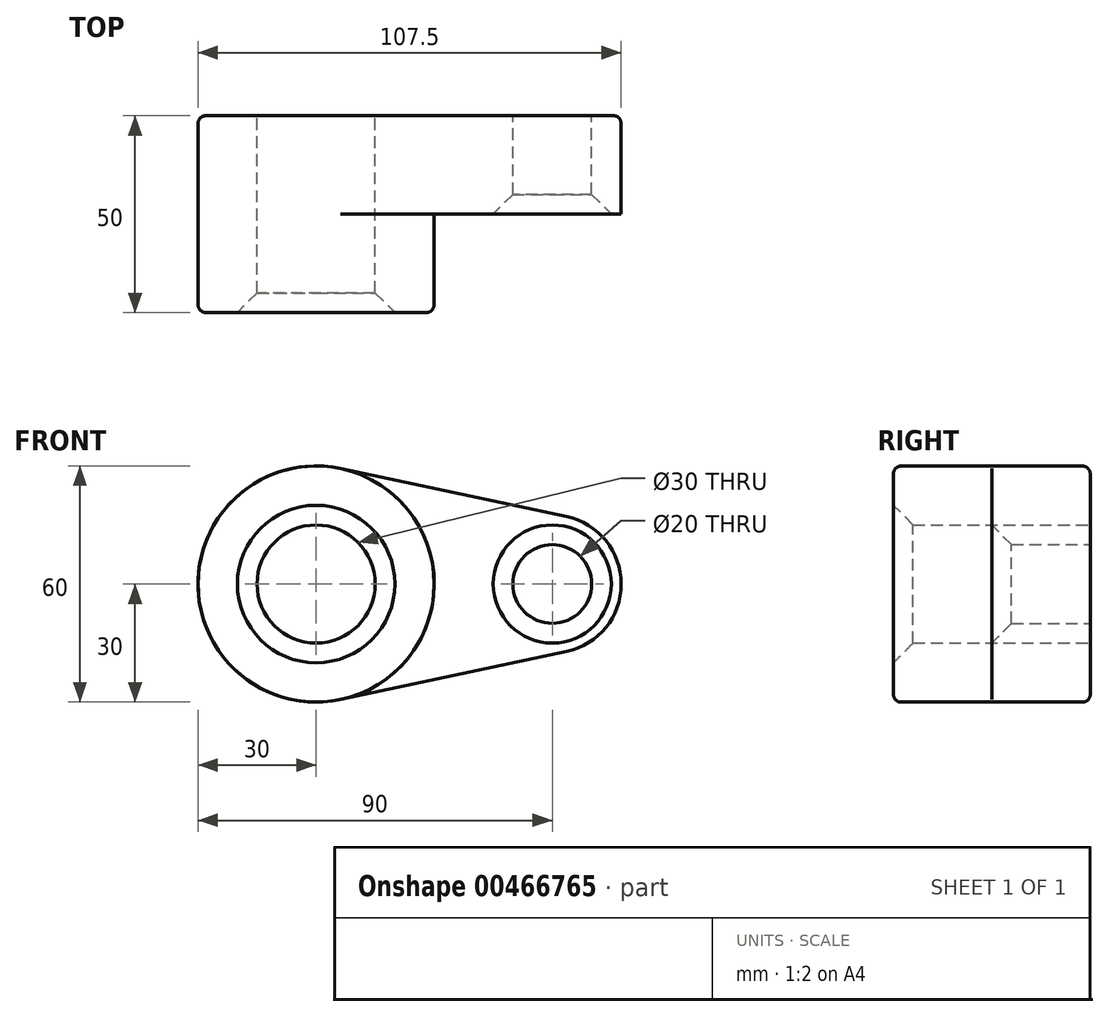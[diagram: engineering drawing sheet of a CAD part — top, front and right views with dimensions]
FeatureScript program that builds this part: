
annotation { "Feature Type Name" : "Feature", "Feature Type Description" : "" }
export const myFeature = defineFeature(function(context is Context, id is Id, definition is map)
    precondition{}
    {
        {
            var Q0;
            Q0=qCreatedBy(makeId("Front.planeOp"),FACE);
            var sketch = newSketch(context, id + "F0", { "sketchPlane" : qUnion([Q0])});
            skCircle(sketch, "E0", {"center": v(0, 0) * mm, "radius": 30 * mm});
            skCircle(sketch, "E1", {"center": v(60, 0) * mm, "radius": 17.5 * mm});
            skLineSegment(sketch, "E2", {"start": v(6.25, 29.34) * mm, "end": v(63.65, 17.12) * mm});
            skLineSegment(sketch, "E3", {"start": v(6.25, -29.34) * mm, "end": v(63.65, -17.12) * mm});
            skCircle(sketch, "E4", {"center": v(0, 0) * mm, "radius": 15 * mm});
            skCircle(sketch, "E5", {"center": v(60, 0) * mm, "radius": 10 * mm});
            skSolve(sketch);
        }
        {
            var Q0;
            Q0=makeQuery(id+"F0.imprint","IMPRINT",FACE,{"disambiguationData":[TD([[makeQuery(id+"F0.imprint","IMPRINT",EDGE,{"derivedFrom":sQuery(id+"F0.wireOp",EDGE,"E4")}),-1.0]])]});
            var Q1;
            {var subQ0=sQuery(id+"F0.wireOp",EDGE,"E2");Q1=makeQuery(id+"F0.imprint","IMPRINT",FACE,{"disambiguationData":[TD([[makeQuery(id+"F0.imprint","IMPRINT",EDGE,{"derivedFrom":subQ0}),-1.0]])]});}
            var Q2;
            Q2=makeQuery(id+"F0.imprint","IMPRINT",FACE,{"disambiguationData":[TD([[makeQuery(id+"F0.imprint","IMPRINT",EDGE,{"derivedFrom":sQuery(id+"F0.wireOp",EDGE,"E5")}),-1.0]])]});
            extrude(context, id + "F1", {"entities" : qUnion([Q0, Q1, Q2]), "depth" : 25 * mm});
        }
        {
            var Q0;
            Q0=makeQuery(id+"F0.imprint","IMPRINT",FACE,{"disambiguationData":[TD([[makeQuery(id+"F0.imprint","IMPRINT",EDGE,{"derivedFrom":sQuery(id+"F0.wireOp",EDGE,"E4")}),-1.0]])]});
            extrude(context, id + "F2", {"entities" : qUnion([Q0]), "operationType" : NewBodyOperationType.ADD, "depth" : 50 * mm});
        }
        {
            var Q0;
            Q0=makeQuery(id+"F2.opExtrude","CAP_EDGE",EDGE,{"disambiguationData":[OSD([sQuery(id+"F0.wireOp",EDGE,"E0")])],"isStart":false});
            var Q1;
            Q1=makeQuery(id+"F1.opExtrude","CAP_EDGE",EDGE,{"disambiguationData":[OSD([sQuery(id+"F0.wireOp",EDGE,"E3")])],"isStart":true});
            fillet(context, id + "F3", {"entities" : qUnion([Q0, Q1]), "radius" : 2 * mm, "tangentPropagation" : true, "allowEdgeOverflow" : false});
        }
        {
            var Q0;
            Q0=makeQuery(id+"F2.opExtrude","CAP_EDGE",EDGE,{"disambiguationData":[OSD([sQuery(id+"F0.wireOp",EDGE,"E4")])],"isStart":false});
            var Q1;
            Q1=makeQuery(id+"F1.opExtrude","CAP_EDGE",EDGE,{"disambiguationData":[OSD([sQuery(id+"F0.wireOp",EDGE,"E5")])],"isStart":false});
            chamfer(context, id + "F4", {"entities" : qUnion([Q0, Q1]), "width" : 5 * mm, "tangentPropagation" : true});
        }
    });
